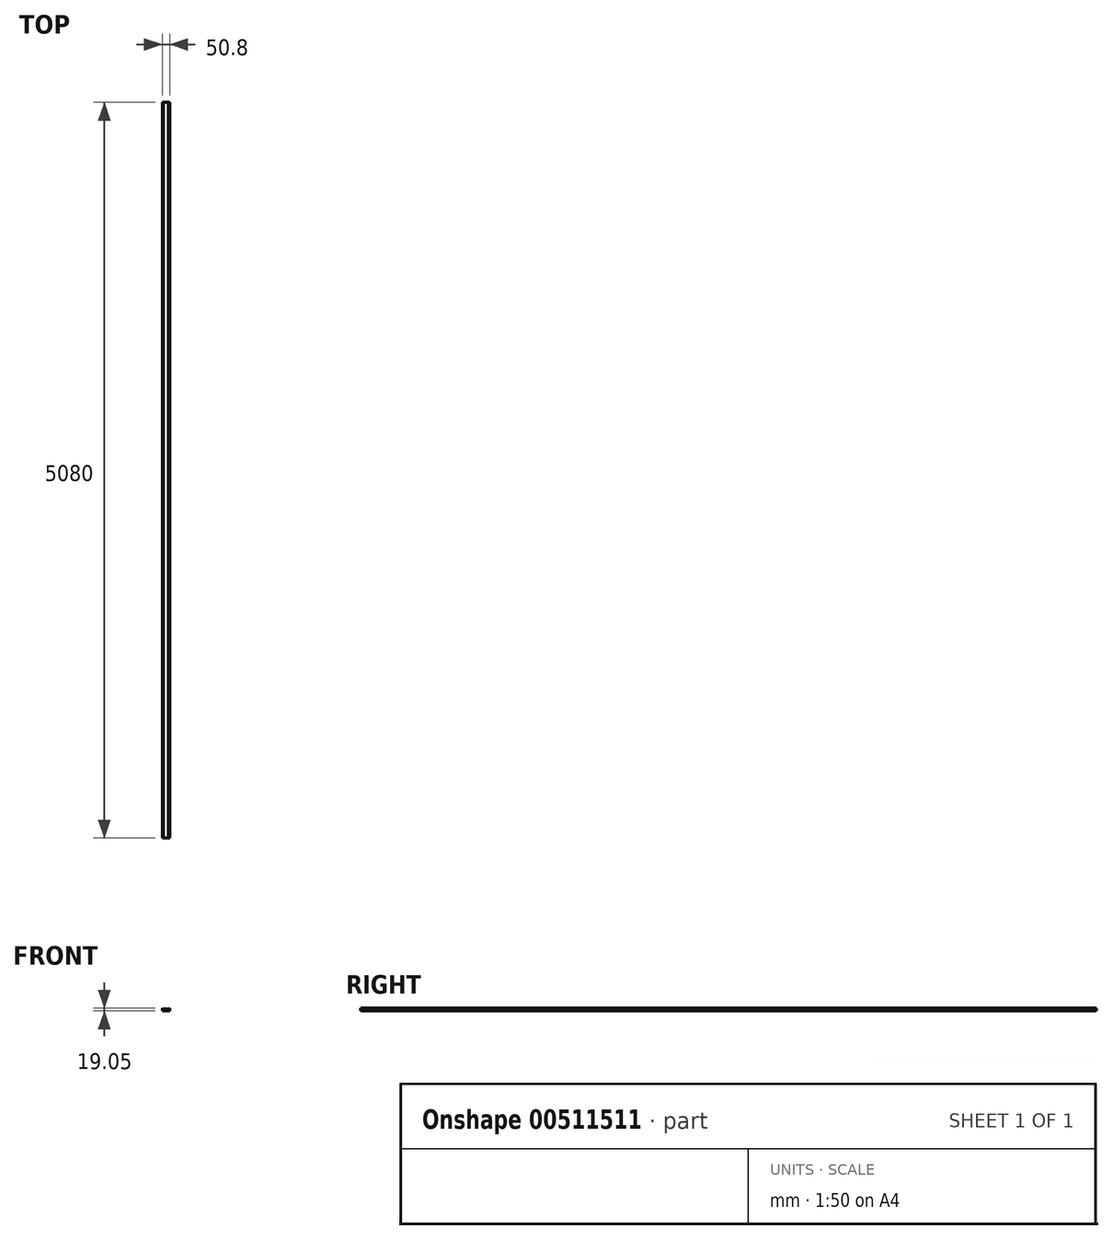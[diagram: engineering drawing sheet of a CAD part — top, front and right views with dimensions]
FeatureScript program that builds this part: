
annotation { "Feature Type Name" : "Feature", "Feature Type Description" : "" }
export const myFeature = defineFeature(function(context is Context, id is Id, definition is map)
    precondition{}
    {
        {
            var Q0;
            Q0=qCreatedBy(makeId("Front.planeOp"),FACE);
            var sketch = newSketch(context, id + "F0", { "sketchPlane" : qUnion([Q0])});
            skLineSegment(sketch, "E0", {"start": v(-25.4, 0) * mm, "end": v(25.4, 0) * mm});
            skLineSegment(sketch, "E1", {"start": v(25.4, 0) * mm, "end": v(25.4, 19.05) * mm});
            skLineSegment(sketch, "E2", {"start": v(25.4, 19.05) * mm, "end": v(15.87, 12.7) * mm});
            skLineSegment(sketch, "E3", {"start": v(15.87, 12.7) * mm, "end": v(-15.87, 12.7) * mm});
            skLineSegment(sketch, "E4", {"start": v(-15.87, 12.7) * mm, "end": v(-25.4, 19.05) * mm});
            skLineSegment(sketch, "E5", {"start": v(-25.4, 19.05) * mm, "end": v(-25.4, 0) * mm});
            skSolve(sketch);
        }
        {
            var Q0;
            Q0 = qSketchRegion(id + "F0", true);
            extrude(context, id + "F1", {"entities" : qUnion([Q0]), "oppositeDirection" : true, "depth" : 5080 * mm, "offsetDistance" : 25.4 * mm});
        }
    });
